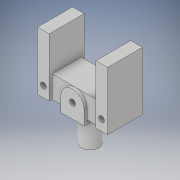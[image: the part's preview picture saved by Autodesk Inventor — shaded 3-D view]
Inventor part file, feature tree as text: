
AUTODESK INVENTOR PART (.ipt)
format: ipt  version: 2019 (Build 230136000, 136)  size: 199,168 bytes
history: native  units: mm
features: sketch x11, extrude x10, plane x2, other x1, projected_geometry x1
ambient origin geometry x8: Origin, YZ Plane, XZ Plane, XY Plane, X Axis, Y Axis, Z Axis, Center Point
bodies: Body1 (feature_tree)
feature tree (25):
  other  "Sólido1"
  extrude  "Extrusión1"  Depth=50.0mm TaperAngle=0.0deg
  extrude  "Extrusión2"  Depth=40.0mm
  extrude  "Extrusión3"  Depth=20.0mm
  extrude  "Extrusión4"  Depth=10.0mm
  sketch  "Boceto5"  dims[d10=5.0mm d11=0.0mm d12=5.0mm d13=0.0mm]
  plane  "Plano de trabajo1"
  plane  "Plano de trabajo2"
  extrude  "Extrusión5"  Depth=5.0mm TaperAngle=0.0deg
  extrude  "Extrusión6"  [1 undecoded]
  extrude  "Extrusión7"  Depth=100.0mm TaperAngle=0.0deg
  extrude  "Extrusión8"  Depth=20.0mm TaperAngle=0.0deg
  extrude  "Extrusión9"  Depth=20.0mm TaperAngle=0.0deg
  extrude  "Extrusión10"  Depth=10.0mm
  sketch  "Boceto1"  dims[d0=30.0mm d1=50.0mm d2=0.0mm]
  sketch  "Boceto2"  dims[d3=60.0mm d4=40.0mm]
  sketch  "Boceto3"  dims[d5=5.0mm d6=0.0mm d7=20.0mm]
  sketch  "Boceto4"  dims[d8=20.0mm d9=10.0mm]
  sketch  "Boceto6"  dims[d14=-20.0mm d15=-30.0mm]
  sketch  "Boceto7"  dims[d16=120.0mm d17=0.0mm d18=100.0mm d19=0.0mm]
  sketch  "Boceto8"  dims[d23=100.0mm d24=20.0mm d25=0.0mm]
  sketch  "Boceto9"  dims[d27=10.0mm d28=20.0mm d29=0.0mm]
  sketch  "Boceto10"  dims[d30=20.0mm d31=0.0mm d33=10.0mm]
  projected_geometry  "Contorno proyectado1"
  sketch  "Boceto11"  dims[d34=20.0mm d35=0.0mm]
note: 1 required parameter value undecoded (feature->parameter linkage not recoverable at this tier; creation-order binding heuristic only, values carry confidence <= 0.55)
